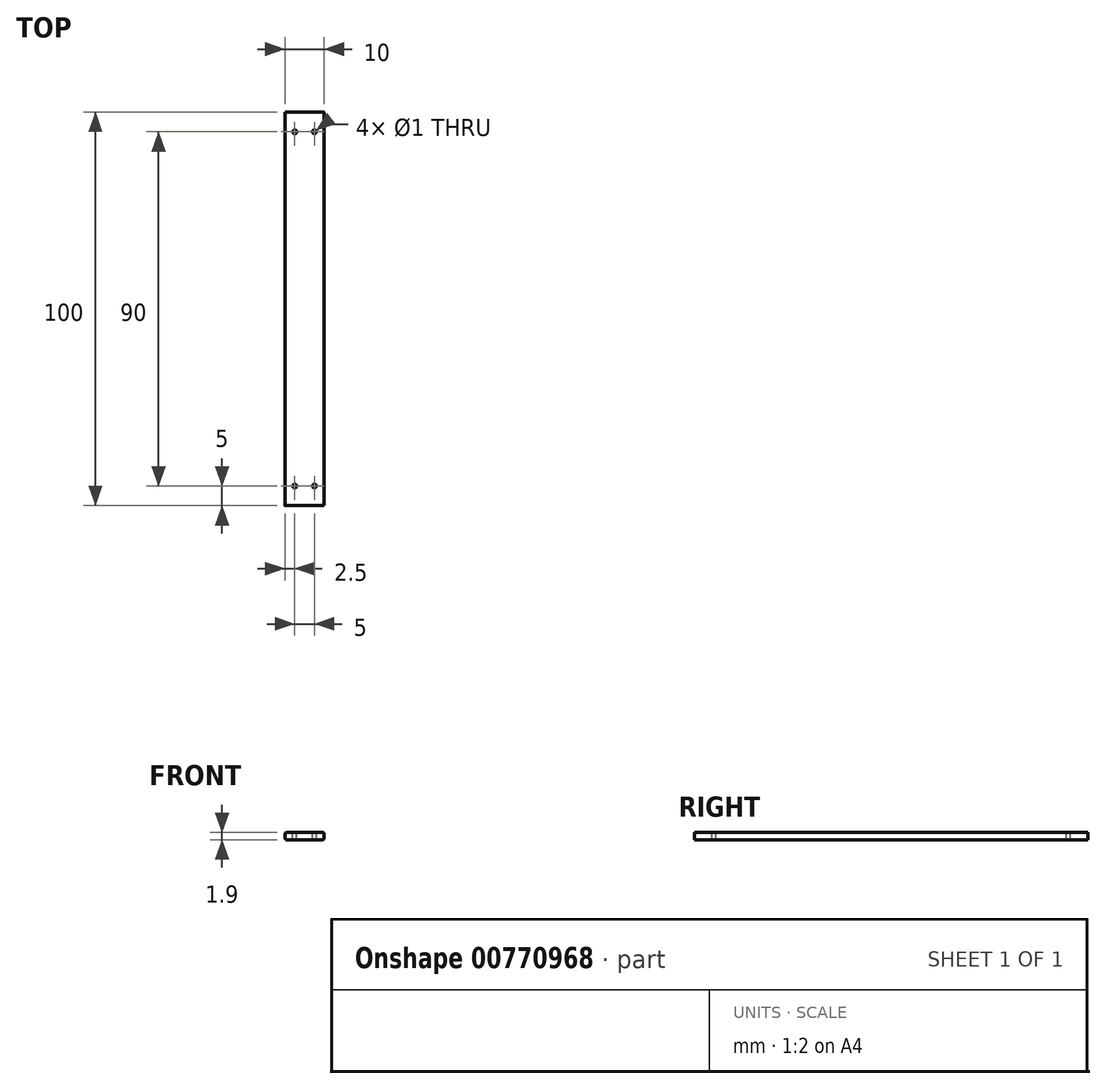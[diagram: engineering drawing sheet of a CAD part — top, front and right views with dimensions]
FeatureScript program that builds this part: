
annotation { "Feature Type Name" : "Feature", "Feature Type Description" : "" }
export const myFeature = defineFeature(function(context is Context, id is Id, definition is map)
    precondition{}
    {
        {
            var Q0;
            Q0=qCreatedBy(makeId("Front.planeOp"),FACE);
            var sketch = newSketch(context, id + "F0", { "sketchPlane" : qUnion([Q0])});
            skLineSegment(sketch, "E0.bottom", {"start": v(-5, 0.95) * mm, "end": v(5, 0.95) * mm});
            skLineSegment(sketch, "E0.top", {"start": v(-5, -0.95) * mm, "end": v(5, -0.95) * mm});
            skLineSegment(sketch, "E0.left", {"start": v(-5, 0.95) * mm, "end": v(-5, -0.95) * mm});
            skLineSegment(sketch, "E0.right", {"start": v(5, 0.95) * mm, "end": v(5, -0.95) * mm});
            skPoint(sketch, "E0.middle", {"position": v(0, 0) * mm});
            skSolve(sketch);
        }
        {
            var Q0;
            Q0=makeQuery(id+"F0.imprint","IMPRINT",FACE,{"disambiguationData":[TD([[makeQuery(id+"F0.imprint","IMPRINT",EDGE,{"derivedFrom":sQuery(id+"F0.wireOp",EDGE,"E0.bottom")}),-1.0]])]});
            extrude(context, id + "F1", {"entities" : qUnion([Q0]), "endBound" : BoundingType.SYMMETRIC, "depth" : 100 * mm, "offsetDistance" : 25 * mm});
        }
        {
            var Q0;
            Q0=makeQuery(id+"F1.opExtrude","SWEPT_FACE",FACE,{"disambiguationData":[OSD([sQuery(id+"F0.wireOp",EDGE,"E0.bottom")])]});
            var sketch = newSketch(context, id + "F2", { "sketchPlane" : qUnion([Q0])});
            skLineSegment(sketch, "E1", {"start": v(5, -50) * mm, "end": v(5, -45) * mm});
            skLineSegment(sketch, "E2", {"start": v(5, -45) * mm, "end": v(2.5, -45) * mm});
            skLineSegment(sketch, "E3", {"start": v(2.5, -45) * mm, "end": v(-2.5, -45) * mm});
            skCircle(sketch, "E4", {"center": v(-2.5, -45) * mm, "radius": 0.5 * mm});
            skCircle(sketch, "E5", {"center": v(2.5, -45) * mm, "radius": 0.5 * mm});
            skLineSegment(sketch, "E6", {"start": v(-5, 50) * mm, "end": v(-5, 45) * mm});
            skLineSegment(sketch, "E7", {"start": v(-5, 45) * mm, "end": v(-2.5, 45) * mm});
            skLineSegment(sketch, "E8", {"start": v(-2.5, 45) * mm, "end": v(2.5, 45) * mm});
            skCircle(sketch, "E9", {"center": v(-2.5, 45) * mm, "radius": 0.5 * mm});
            skCircle(sketch, "E10", {"center": v(2.5, 45) * mm, "radius": 0.5 * mm});
            skSolve(sketch);
        }
        {
            var Q0;
            Q0=sQuery(id+"F2.wireOp",VERTEX,"E7.end");
            var Q1;
            Q1=sQuery(id+"F2.wireOp",VERTEX,"E8.end");
            var Q2;
            Q2=sQuery(id+"F2.wireOp",VERTEX,"E3.end");
            var Q3;
            Q3=sQuery(id+"F2.wireOp",VERTEX,"E2.end");
            var Q4;
            Q4=makeQuery(id+"F1.opExtrude","SWEPT_BODY",BODY,{"disambiguationData":[OSD([sQuery(id+"F0.wireOp",EDGE,"E0.bottom"),sQuery(id+"F0.wireOp",EDGE,"E0.top"),sQuery(id+"F0.wireOp",EDGE,"E0.left"),sQuery(id+"F0.wireOp",EDGE,"E0.right")])]});
            hole(context, id + "F3", {"style" : HoleStyle.SIMPLE, "endStyle" : HoleEndStyle.THROUGH, "holeDiameter" : 1 * mm, "majorDiameter" : 5 * mm, "isTappedThrough" : true, "tappedDepth" : 12 * mm, "tapClearance" : 3, "locations" : qUnion([Q0, Q1, Q2, Q3]), "scope" : qUnion([Q4])});
        }
        {
            var Q0;
            Q0=makeQuery(id+"F1.opExtrude","SWEPT_EDGE",EDGE,{"disambiguationData":[OSD([sQuery(id+"F0.wireOp",EDGE,"E0.bottom"),sQuery(id+"F0.wireOp",EDGE,"E0.right")])]});
            var Q1;
            Q1=makeQuery(id+"F1.opExtrude","SWEPT_EDGE",EDGE,{"disambiguationData":[OSD([sQuery(id+"F0.wireOp",EDGE,"E0.bottom"),sQuery(id+"F0.wireOp",EDGE,"E0.left")])]});
            var Q2;
            Q2=makeQuery(id+"F1.opExtrude","SWEPT_EDGE",EDGE,{"disambiguationData":[OSD([sQuery(id+"F0.wireOp",EDGE,"E0.top"),sQuery(id+"F0.wireOp",EDGE,"E0.right")])]});
            var Q3;
            Q3=makeQuery(id+"F1.opExtrude","SWEPT_EDGE",EDGE,{"disambiguationData":[OSD([sQuery(id+"F0.wireOp",EDGE,"E0.top"),sQuery(id+"F0.wireOp",EDGE,"E0.left")])]});
            fillet(context, id + "F4", {"entities" : qUnion([Q0, Q1, Q2, Q3]), "radius" : 0.5 * mm, "tangentPropagation" : true, "allowEdgeOverflow" : false});
        }
    });
